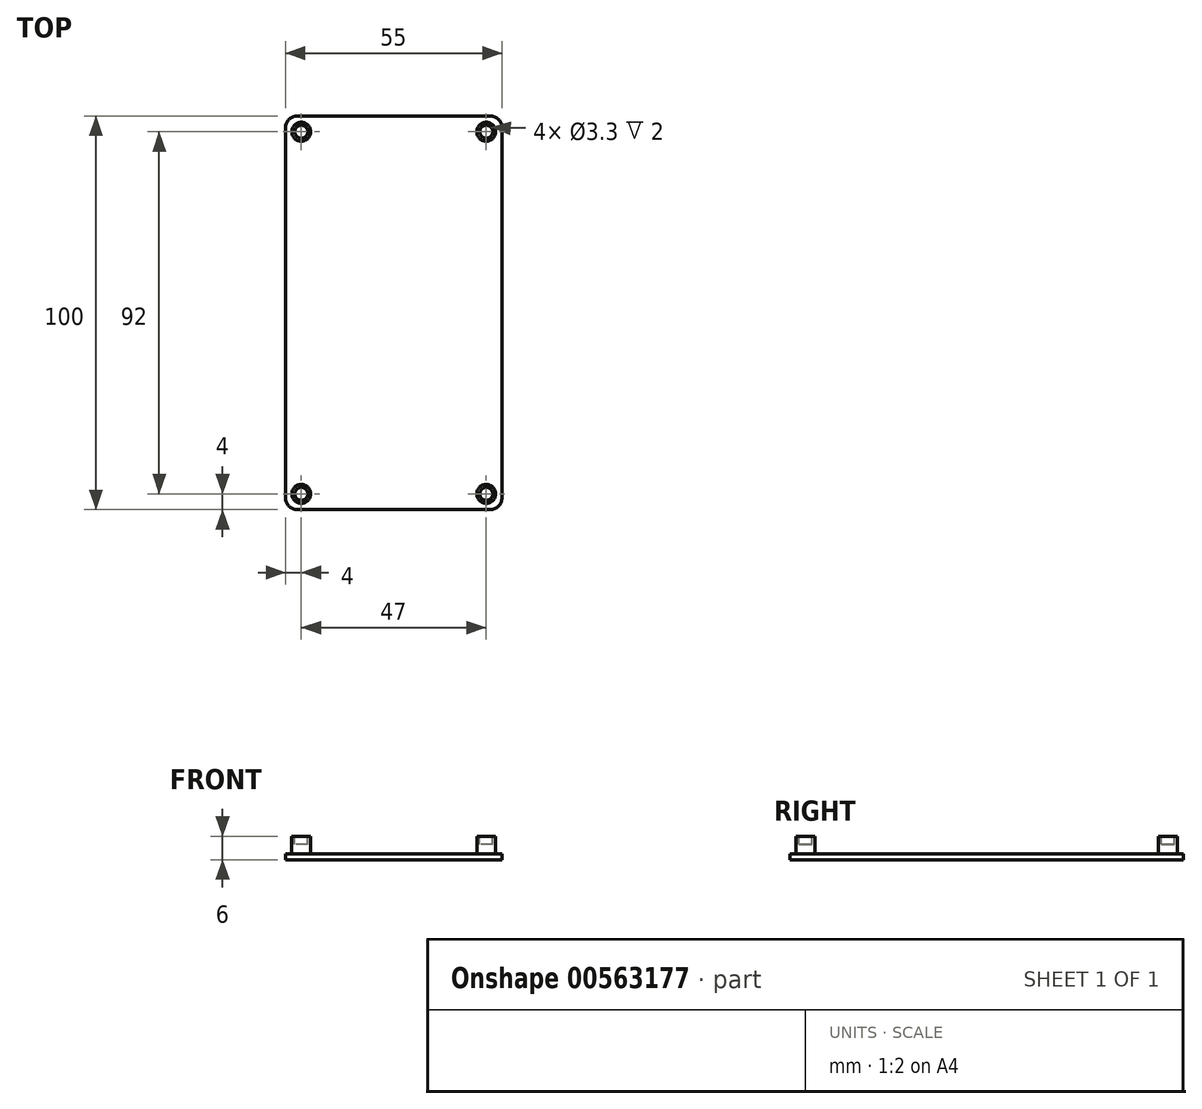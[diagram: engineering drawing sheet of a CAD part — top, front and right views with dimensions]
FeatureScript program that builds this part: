
annotation { "Feature Type Name" : "Feature", "Feature Type Description" : "" }
export const myFeature = defineFeature(function(context is Context, id is Id, definition is map)
    precondition{}
    {
        {
            var Q0;
            Q0=qCreatedBy(makeId("Top.planeOp"),FACE);
            var sketch = newSketch(context, id + "F0", { "sketchPlane" : qUnion([Q0])});
            skLineSegment(sketch, "E0.bottom", {"start": v(0, 0) * mm, "end": v(55, 0) * mm});
            skLineSegment(sketch, "E0.top", {"start": v(0, 100) * mm, "end": v(55, 100) * mm});
            skLineSegment(sketch, "E0.left", {"start": v(0, 0) * mm, "end": v(0, 100) * mm});
            skLineSegment(sketch, "E0.right", {"start": v(55, 0) * mm, "end": v(55, 100) * mm});
            skSolve(sketch);
        }
        {
            var Q0;
            Q0=makeQuery(id+"F0.imprint","IMPRINT",FACE,{"disambiguationData":[TD([[makeQuery(id+"F0.imprint","IMPRINT",EDGE,{"derivedFrom":sQuery(id+"F0.wireOp",EDGE,"E0.bottom")}),1.0]])]});
            extrude(context, id + "F1", {"entities" : qUnion([Q0]), "depth" : 1.5 * mm, "offsetDistance" : 25 * mm});
        }
        {
            var Q0;
            Q0=makeQuery(id+"F1.opExtrude","SWEPT_EDGE",EDGE,{"disambiguationData":[OSD([sQuery(id+"F0.wireOp",EDGE,"E0.top"),sQuery(id+"F0.wireOp",EDGE,"E0.left")])]});
            var Q1;
            Q1=makeQuery(id+"F1.opExtrude","SWEPT_EDGE",EDGE,{"disambiguationData":[OSD([sQuery(id+"F0.wireOp",EDGE,"E0.top"),sQuery(id+"F0.wireOp",EDGE,"E0.right")])]});
            var Q2;
            Q2=makeQuery(id+"F1.opExtrude","SWEPT_EDGE",EDGE,{"disambiguationData":[OSD([sQuery(id+"F0.wireOp",EDGE,"E0.bottom"),sQuery(id+"F0.wireOp",EDGE,"E0.left")])]});
            var Q3;
            Q3=makeQuery(id+"F1.opExtrude","SWEPT_EDGE",EDGE,{"disambiguationData":[OSD([sQuery(id+"F0.wireOp",EDGE,"E0.bottom"),sQuery(id+"F0.wireOp",EDGE,"E0.right")])]});
            fillet(context, id + "F2", {"entities" : qUnion([Q0, Q1, Q2, Q3]), "radius" : 3 * mm, "tangentPropagation" : true, "allowEdgeOverflow" : false});
        }
        {
            var Q0;
            Q0=makeQuery(id+"F1.opExtrude","CAP_FACE",FACE,{"disambiguationData":[OSD([sQuery(id+"F0.wireOp",EDGE,"E0.bottom"),sQuery(id+"F0.wireOp",EDGE,"E0.top"),sQuery(id+"F0.wireOp",EDGE,"E0.left"),sQuery(id+"F0.wireOp",EDGE,"E0.right")])],"isStart":false});
            var sketch = newSketch(context, id + "F3", { "sketchPlane" : qUnion([Q0])});
            skCircle(sketch, "E1", {"center": v(4, 96) * mm, "radius": 2.4 * mm});
            skCircle(sketch, "E2.0.1.0", {"center": v(4, 4) * mm, "radius": 2.4 * mm});
            skCircle(sketch, "E2.1.0.0", {"center": v(51, 96) * mm, "radius": 2.4 * mm});
            skCircle(sketch, "E2.1.1.0", {"center": v(51, 4) * mm, "radius": 2.4 * mm});
            skLineSegment(sketch, "E2.direction1", {"start": v(4, 96) * mm, "end": v(51, 96) * mm, "construction": true});
            skLineSegment(sketch, "E2.direction2", {"start": v(4, 96) * mm, "end": v(4, 4) * mm, "construction": true});
            skSolve(sketch);
        }
        {
            var Q0;
            Q0 = qSketchRegion(id + "F3", true);
            extrude(context, id + "F4", {"entities" : qUnion([Q0]), "operationType" : NewBodyOperationType.ADD, "depth" : 4.5 * mm, "offsetDistance" : 25 * mm});
        }
        {
            var Q0;
            Q0=makeQuery(id+"F4.opExtrude","CAP_FACE",FACE,{"disambiguationData":[OSD([sQuery(id+"F3.wireOp",EDGE,"E1")])],"isStart":false});
            var sketch = newSketch(context, id + "F5", { "sketchPlane" : qUnion([Q0])});
            skCircle(sketch, "E3", {"center": v(4, 96) * mm, "radius": 1.65 * mm});
            skCircle(sketch, "E4.0.1.0", {"center": v(4, 4) * mm, "radius": 1.65 * mm});
            skCircle(sketch, "E4.1.0.0", {"center": v(51, 96) * mm, "radius": 1.65 * mm});
            skCircle(sketch, "E4.1.1.0", {"center": v(51, 4) * mm, "radius": 1.65 * mm});
            skLineSegment(sketch, "E4.direction1", {"start": v(4, 96) * mm, "end": v(51, 96) * mm, "construction": true});
            skLineSegment(sketch, "E4.direction2", {"start": v(4, 96) * mm, "end": v(4, 4) * mm, "construction": true});
            skSolve(sketch);
        }
        {
            var Q0;
            Q0 = qSketchRegion(id + "F5", true);
            extrude(context, id + "F6", {"entities" : qUnion([Q0]), "operationType" : NewBodyOperationType.REMOVE, "oppositeDirection" : true, "depth" : 2 * mm, "offsetDistance" : 25 * mm});
        }
    });
